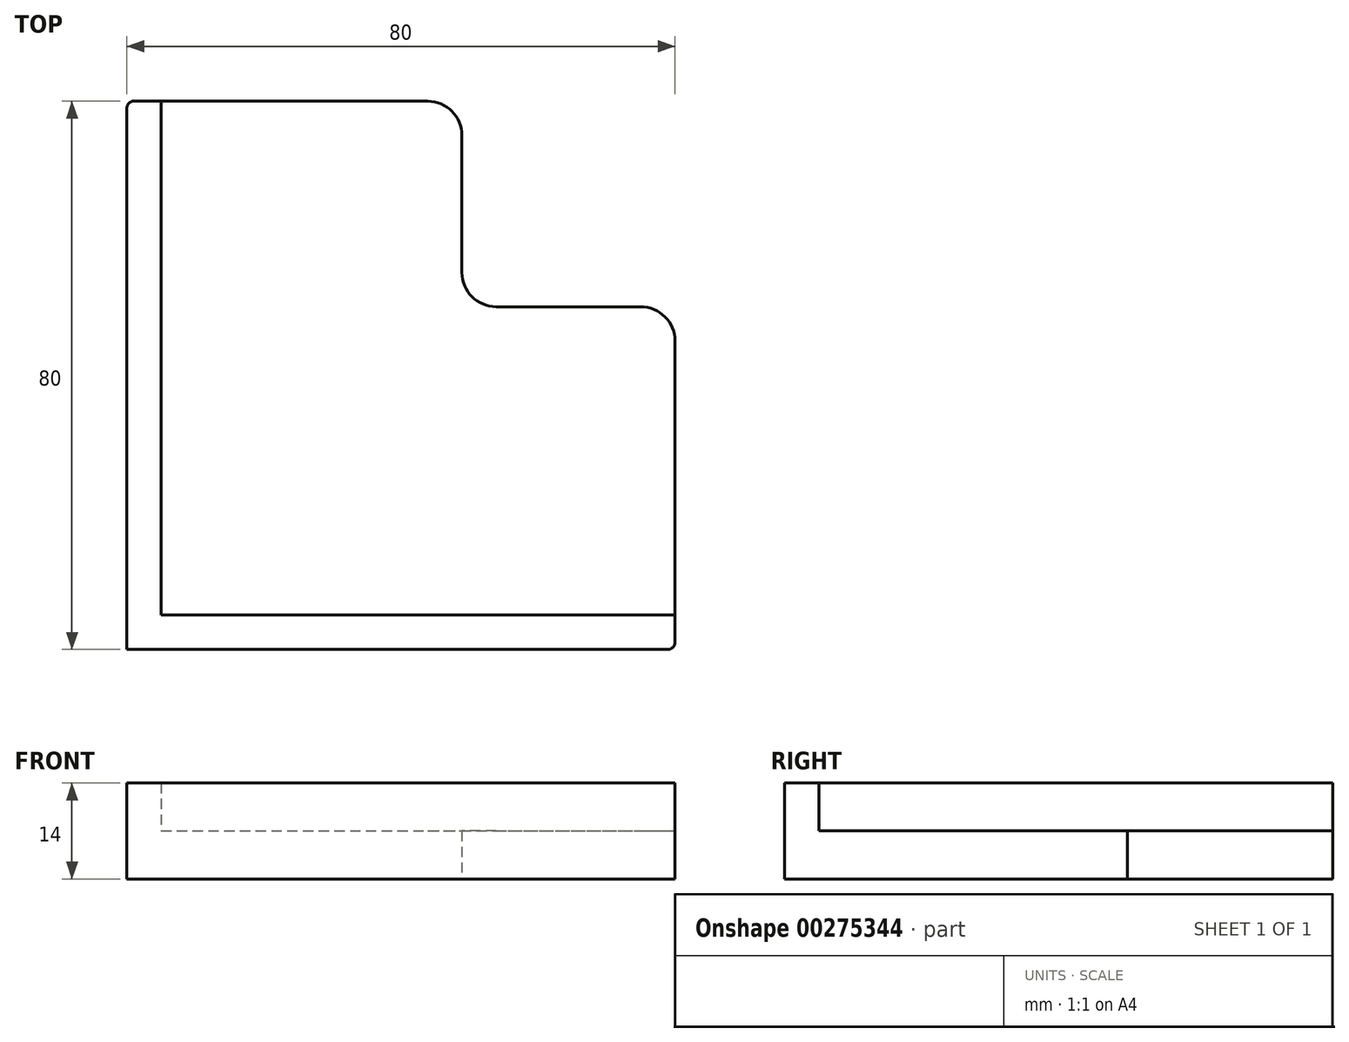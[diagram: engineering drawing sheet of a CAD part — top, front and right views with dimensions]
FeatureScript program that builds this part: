
annotation { "Feature Type Name" : "Feature", "Feature Type Description" : "" }
export const myFeature = defineFeature(function(context is Context, id is Id, definition is map)
    precondition{}
    {
        {
            var Q0;
            Q0=qCreatedBy(makeId("Top.planeOp"),FACE);
            var sketch = newSketch(context, id + "F0", { "sketchPlane" : qUnion([Q0])});
            skLineSegment(sketch, "E0", {"start": v(-54.23, 39.63) * mm, "end": v(-54.23, -40.37) * mm});
            skLineSegment(sketch, "E1", {"start": v(-54.23, -40.37) * mm, "end": v(25.77, -40.37) * mm});
            skLineSegment(sketch, "E2", {"start": v(-54.23, 39.63) * mm, "end": v(-41.23, 39.63) * mm});
            skLineSegment(sketch, "E3", {"start": v(25.77, -40.37) * mm, "end": v(25.77, -27.37) * mm});
            skLineSegment(sketch, "E4", {"start": v(25.77, -27.37) * mm, "end": v(-41.23, -27.37) * mm});
            skLineSegment(sketch, "E5", {"start": v(-41.23, -27.37) * mm, "end": v(-41.23, 39.63) * mm});
            skSolve(sketch);
        }
        {
            var Q0;
            Q0 = qSketchRegion(id + "F0", true);
            extrude(context, id + "F1", {"entities" : qUnion([Q0]), "oppositeDirection" : true, "depth" : 80 * mm});
        }
        {
            var Q0;
            Q0=makeQuery(id+"F1.opExtrude","CAP_FACE",FACE,{"disambiguationData":[OSD([sQuery(id+"F0.wireOp",EDGE,"E0"),sQuery(id+"F0.wireOp",EDGE,"E1"),sQuery(id+"F0.wireOp",EDGE,"E2"),sQuery(id+"F0.wireOp",EDGE,"E3"),sQuery(id+"F0.wireOp",EDGE,"E4"),sQuery(id+"F0.wireOp",EDGE,"E5")])],"isStart":true});
            var sketch = newSketch(context, id + "F2", { "sketchPlane" : qUnion([Q0])});
            skLineSegment(sketch, "E6", {"start": v(-51.23, 39.63) * mm, "end": v(-51.23, -37.37) * mm});
            skLineSegment(sketch, "E7", {"start": v(-51.23, -37.37) * mm, "end": v(25.77, -37.37) * mm});
            skLineSegment(sketch, "E8", {"start": v(25.77, -37.37) * mm, "end": v(25.77, -30.37) * mm});
            skLineSegment(sketch, "E9", {"start": v(25.77, -30.37) * mm, "end": v(-44.23, -30.37) * mm});
            skLineSegment(sketch, "E10", {"start": v(-44.23, -30.37) * mm, "end": v(-44.23, 39.63) * mm});
            skLineSegment(sketch, "E11", {"start": v(-44.23, 39.63) * mm, "end": v(-51.23, 39.63) * mm});
            skSolve(sketch);
        }
        {
            var Q0;
            Q0 = qSketchRegion(id + "F2", true);
            extrude(context, id + "F3", {"entities" : qUnion([Q0]), "operationType" : NewBodyOperationType.REMOVE, "oppositeDirection" : true, "depth" : 75 * mm});
        }
        {
            var Q0;
            Q0=makeQuery(id+"F1.opExtrude","SWEPT_FACE",FACE,{"disambiguationData":[OSD([sQuery(id+"F0.wireOp",EDGE,"E3")])]});
            var sketch = newSketch(context, id + "F4", { "sketchPlane" : qUnion([Q0])});
            skLineSegment(sketch, "E12.bottom", {"start": v(-40.37, -80) * mm, "end": v(-27.37, -80) * mm});
            skLineSegment(sketch, "E12.top", {"start": v(-40.37, -80) * mm, "end": v(-27.37, -80) * mm});
            skLineSegment(sketch, "E12.left", {"start": v(-40.37, -80) * mm, "end": v(-40.37, -80) * mm});
            skLineSegment(sketch, "E12.right", {"start": v(-27.37, -80) * mm, "end": v(-27.37, -80) * mm});
            skLineSegment(sketch, "E13.bottom", {"start": v(-20.37, -80) * mm, "end": v(-40.37, -80) * mm});
            skLineSegment(sketch, "E13.top", {"start": v(9.63, -97) * mm, "end": v(-40.37, -97) * mm});
            skLineSegment(sketch, "E13.right", {"start": v(-40.37, -80) * mm, "end": v(-40.37, -97) * mm});
            skLineSegment(sketch, "E14", {"start": v(-35.37, -83) * mm, "end": v(-35.37, -90) * mm});
            skLineSegment(sketch, "E15", {"start": v(-35.37, -90) * mm, "end": v(9.63, -90) * mm});
            skLineSegment(sketch, "E16", {"start": v(9.63, -90) * mm, "end": v(9.63, -97) * mm});
            skLineSegment(sketch, "E17", {"start": v(-20.37, -80) * mm, "end": v(-20.37, -83) * mm});
            skLineSegment(sketch, "E18", {"start": v(-20.37, -83) * mm, "end": v(-35.37, -83) * mm});
            skSolve(sketch);
        }
        {
            var Q0;
            Q0 = qSketchRegion(id + "F4", true);
            extrude(context, id + "F5", {"entities" : qUnion([Q0]), "operationType" : NewBodyOperationType.ADD, "oppositeDirection" : true, "depth" : 80 * mm});
        }
        {
            var Q0;
            Q0=makeQuery(id+"F1.opExtrude","SWEPT_FACE",FACE,{"disambiguationData":[OSD([sQuery(id+"F0.wireOp",EDGE,"E2")])]});
            var sketch = newSketch(context, id + "F6", { "sketchPlane" : qUnion([Q0])});
            skLineSegment(sketch, "E19.bottom", {"start": v(34.23, -80) * mm, "end": v(54.23, -80) * mm});
            skLineSegment(sketch, "E19.top", {"start": v(41.23, -97) * mm, "end": v(54.23, -97) * mm});
            skLineSegment(sketch, "E19.right", {"start": v(54.23, -80) * mm, "end": v(54.23, -97) * mm});
            skLineSegment(sketch, "E20", {"start": v(34.23, -80) * mm, "end": v(34.23, -83) * mm});
            skLineSegment(sketch, "E21", {"start": v(34.23, -83) * mm, "end": v(49.23, -83) * mm});
            skLineSegment(sketch, "E22", {"start": v(49.23, -83) * mm, "end": v(49.23, -90) * mm});
            skLineSegment(sketch, "E23", {"start": v(49.23, -90) * mm, "end": v(5.33, -90) * mm});
            skLineSegment(sketch, "E24", {"start": v(5.33, -90) * mm, "end": v(5.33, -97) * mm});
            skLineSegment(sketch, "E25", {"start": v(5.33, -97) * mm, "end": v(41.23, -97) * mm});
            skSolve(sketch);
        }
        {
            var Q0;
            Q0 = qSketchRegion(id + "F6", true);
            extrude(context, id + "F7", {"entities" : qUnion([Q0]), "operationType" : NewBodyOperationType.ADD, "oppositeDirection" : true, "depth" : 80 * mm});
        }
        {
            var Q0;
            Q0=makeQuery(id+"F7.boolean.opBoolean","MERGE",FACE,{"derivedFrom":[makeQuery(id+"F5.opExtrude","SWEPT_FACE",FACE,{"disambiguationData":[OSD([sQuery(id+"F4.wireOp",EDGE,"E18")])]}),makeQuery(id+"F7.opExtrude","SWEPT_FACE",FACE,{"disambiguationData":[OSD([sQuery(id+"F6.wireOp",EDGE,"E21")])]})]});
            cPlane(context, id + "F8", {"entities" : qUnion([Q0]), "cplaneType" : CPlaneType.OFFSET, "offset" : 0 * mm, "oppositeDirection" : true, "width" : 150 * mm, "height" : 150 * mm});
        }
        {
            var Q0;
            Q0=qCreatedBy(id+"F8.planeOp",FACE);
            var sketch = newSketch(context, id + "F9", { "sketchPlane" : qUnion([Q0])});
            skLineSegment(sketch, "E26.bottom", {"start": v(52.95, 67.54) * mm, "end": v(-62.43, 67.54) * mm});
            skLineSegment(sketch, "E26.top", {"start": v(52.95, -73.8) * mm, "end": v(-62.43, -73.8) * mm});
            skLineSegment(sketch, "E26.left", {"start": v(52.95, 67.54) * mm, "end": v(52.95, -73.8) * mm});
            skLineSegment(sketch, "E26.right", {"start": v(-62.43, 67.54) * mm, "end": v(-62.43, -73.8) * mm});
            skSolve(sketch);
        }
        {
            var Q0;
            Q0=makeQuery(id+"F9.imprint","IMPRINT",FACE,{"disambiguationData":[TD([[makeQuery(id+"F9.imprint","IMPRINT",EDGE,{"derivedFrom":sQuery(id+"F9.wireOp",EDGE,"E26.bottom")}),1.0]])]});
            extrude(context, id + "F10", {"entities" : qUnion([Q0]), "operationType" : NewBodyOperationType.REMOVE, "oppositeDirection" : true, "depth" : 97.9 * mm});
        }
        {
            var Q0;
            Q0=makeQuery(id+"F7.boolean.opBoolean","INTERSECT",EDGE,{"derivedFrom":[makeQuery(id+"F5.opExtrude","SWEPT_FACE",FACE,{"disambiguationData":[OSD([sQuery(id+"F4.wireOp",EDGE,"E16")])]}),makeQuery(id+"F7.opExtrude","SWEPT_FACE",FACE,{"disambiguationData":[OSD([sQuery(id+"F6.wireOp",EDGE,"E24")])]})]});
            var Q1;
            Q1=makeQuery(id+"F7.opExtrude","CAP_EDGE",EDGE,{"disambiguationData":[OSD([sQuery(id+"F6.wireOp",EDGE,"E24")])],"isStart":true});
            var Q2;
            Q2=makeQuery(id+"F5.opExtrude","CAP_EDGE",EDGE,{"disambiguationData":[OSD([sQuery(id+"F4.wireOp",EDGE,"E16")])],"isStart":true});
            fillet(context, id + "F11", {"entities" : qUnion([Q0, Q1, Q2]), "radius" : 5 * mm, "tangentPropagation" : true, "allowEdgeOverflow" : false});
        }
        {
            var Q0;
            Q0=makeQuery(id+"F5.boolean.opBoolean","MERGE",EDGE,{"derivedFrom":[makeQuery(id+"F1.opExtrude","SWEPT_EDGE",EDGE,{"disambiguationData":[OSD([sQuery(id+"F0.wireOp",EDGE,"E1"),sQuery(id+"F0.wireOp",EDGE,"E3")])]}),makeQuery(id+"F5.opExtrude","CAP_EDGE",EDGE,{"disambiguationData":[OSD([sQuery(id+"F4.wireOp",EDGE,"E13.right")])],"isStart":true})]});
            var Q1;
            Q1=makeQuery(id+"F7.boolean.opBoolean","MERGE",EDGE,{"derivedFrom":[makeQuery(id+"F1.opExtrude","SWEPT_EDGE",EDGE,{"disambiguationData":[OSD([sQuery(id+"F0.wireOp",EDGE,"E0"),sQuery(id+"F0.wireOp",EDGE,"E2")])]}),makeQuery(id+"F7.opExtrude","CAP_EDGE",EDGE,{"disambiguationData":[OSD([sQuery(id+"F6.wireOp",EDGE,"E19.right")])],"isStart":true})]});
            fillet(context, id + "F12", {"entities" : qUnion([Q0, Q1]), "radius" : 1 * mm, "tangentPropagation" : true, "allowEdgeOverflow" : false});
        }
    });
